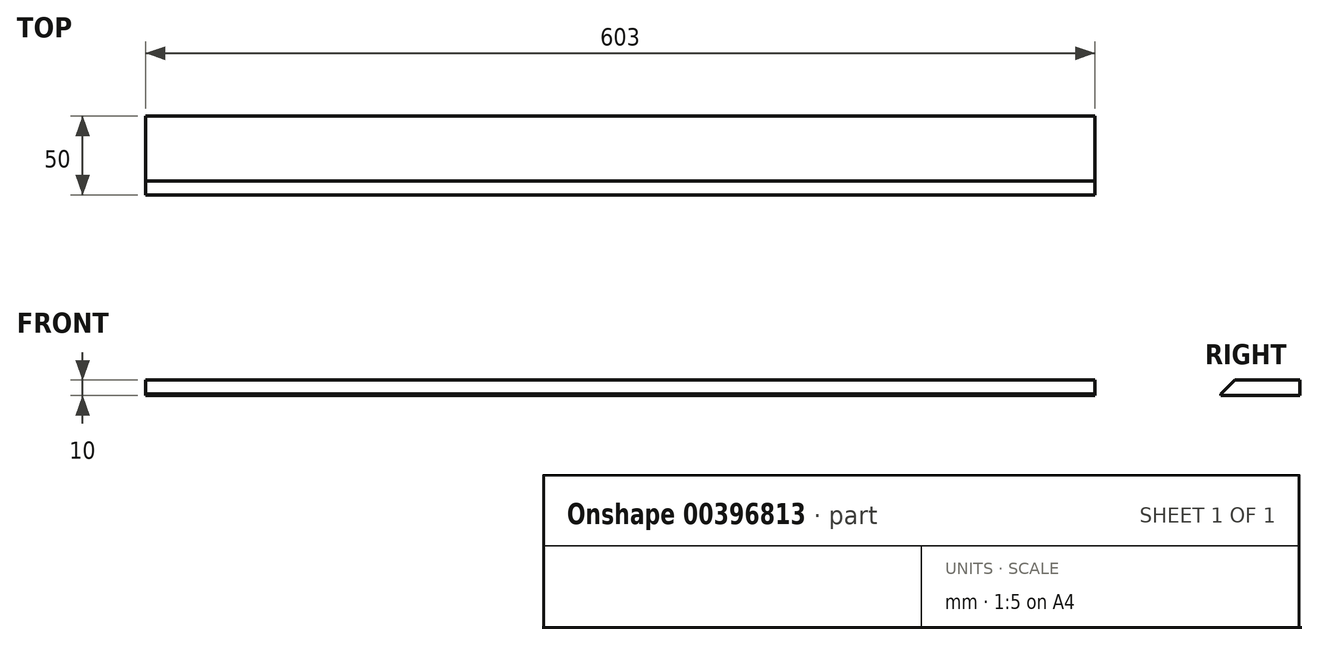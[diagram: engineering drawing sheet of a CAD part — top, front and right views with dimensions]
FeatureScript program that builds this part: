
annotation { "Feature Type Name" : "Feature", "Feature Type Description" : "" }
export const myFeature = defineFeature(function(context is Context, id is Id, definition is map)
    precondition{}
    {
        {
            var Q0;
            Q0=qCreatedBy(makeId("Right.planeOp"),FACE);
            var sketch = newSketch(context, id + "F0", { "sketchPlane" : qUnion([Q0])});
            skLineSegment(sketch, "E0.bottom", {"start": v(-25, 0) * mm, "end": v(25, 0) * mm});
            skLineSegment(sketch, "E0.top", {"start": v(-25, 10) * mm, "end": v(25, 10) * mm});
            skLineSegment(sketch, "E0.left", {"start": v(-25, 0) * mm, "end": v(-25, 10) * mm});
            skLineSegment(sketch, "E0.right", {"start": v(25, 0) * mm, "end": v(25, 10) * mm});
            skSolve(sketch);
        }
        {
            var Q0;
            Q0=makeQuery(id+"F0.imprint","IMPRINT",FACE,{"disambiguationData":[TD([[makeQuery(id+"F0.imprint","IMPRINT",EDGE,{"derivedFrom":sQuery(id+"F0.wireOp",EDGE,"E0.bottom")}),1.0]])]});
            extrude(context, id + "F1", {"entities" : qUnion([Q0]), "endBound" : BoundingType.SYMMETRIC, "depth" : 603 * mm});
        }
        {
            var Q0;
            Q0=makeQuery(id+"F1.opExtrude","SWEPT_EDGE",EDGE,{"disambiguationData":[OSD([sQuery(id+"F0.wireOp",EDGE,"E0.top"),sQuery(id+"F0.wireOp",EDGE,"E0.left")])]});
            chamfer(context, id + "F2", {"entities" : qUnion([Q0]), "width" : 9 * mm, "tangentPropagation" : true});
        }
    });
